# Revit family: Camera-Security-Panasonic-Super_Dynamic-Weatherproof-Network-S1570LSeriesX
name_source: partatom
category: Security Devices
revit_build: Autodesk Revit 2016 (Build: 20150220_1215(x64)
units: mm (PartAtom-declared; Revit-internal decimal feet)

## family parameters
Cut with Voids When Loaded = No
Host = Face
Maintain Annotation Orientation = No
OmniClass Number = 23.85.10.14.11
OmniClass Title = Cameras
Part Type = Normal
Room Calculation Point = No
Round Connector Dimension = Use Diameter
Shared = No

## types (1)
- WV-S1570L
    4K = Resolution : 4K
    Alarm Input Or Output Specification = ALARM IN 1(Alarm input 1/ Black & white input/ Auto time adjustment input) (x1), ALARM IN 2 (Alarm input 2/ ALARM OUT) (x1), ALARM IN 3 (Alarm input 3/ AUX OUT) (x1)
    Angle Of View = 104
    Aspect169 = Yes
    Audio In = Yes
    Audio Out = Yes
    Communication Ports = 10Base-T / 100Base-TX, RJ45 connector
    Date Last Modified = 2019/05/14
    Day Or Night = Yes
    Default Elevation = 0 "
    Description = Security Camera, Super Dynamic, 4K, Weatherproof, Network, WV-S1570L
    Equipment Abbreviation = SC
    Family Version = 1.0.0
    Full HD = Resolution : Full HD
    HFOV Max 169 = 104.00°
    HFOV Max 43 = 104.00°
    HFOV Min 169 = 53.00°
    HFOV Min 43 = 53.00°
    Has POE = Yes
    IP Or Analog = IP
    Indoor Or Outdoor = Outdoor
    Manufacturer = Panasonic
    Minimum Illumination = 0.090 lx
    Model = WV-S1570L
    Model Disclaimer = Contact Panasonic for more information
    Mounting Positions = Mount Dependent or Surface Mount
    Operational Humidity = 10 to 100 % (no condensation)
    Operational Temperature = -40 °F to 140 °F
    Panning Range = -180 to +180
    Part Description = Security Camera, Super Dynamic, 4K, Weatherproof, Network, WV-S1570L
    Part Number = WV-S1570L
    Power Active = 10.0 W
    Product Documentation Link = https://bizpartner.panasonic.net
    Product Material = Paint - Panasonic - Silver
    Product Page URL = https://security.panasonic.com
    Provide Feedback = https://www.surveymonkey.com
    Regulatory Compliance = UL (UL60950-1), c-UL (CSA C22.2 No.60950-1), CE, IEC60950-1, FCC (Part15 ClassA), ICES003 ClassA, EN55032 ClassB, EN55024
    Shock Resistance = IK10 (IEC 62262)
    Storage Temperature = -40 °F to 140 °F
    Super Dynamic Range = Yes
    Tilting Range = -100 to +100
    URL = http://security.panasonic.com
    VFOV Max 169 = 56.00°
    VFOV Max 43 = 56.00°
    VFOV Min 169 = 30.00°
    VFOV Min 43 = 30.00°
    Vandal Resistant = Yes
    Voltage DC = 12 V
    WQHD = Resolution : WQHD
    Water and Dust Resistance = IP66 (IEC60529), Type 4X (UL50E), NEMA 4X compliant
    Width = 5.23622 "
    Yaw Max = 100.00°
    Yaw Min = -190.00°
    Yawing Range = -190 to +100
    z Base Square = Yes
    z Camera Center Offset = 0.2874 "
    z Camera Center Offset Base = 1.1811 "
    z Column Height = 3.11024 "
    z Const CameraYawAxis = 15.74803 "
    z Const Pan Handle Length = 27.55906 "
    z Const Tilt Base Length = 9.84252 "
    z Const Tilt Base2 Length = 19.68504 "
    z Const Tilt Handle Length = 14.17323 "
    z Const Yaw Axis Length = 7.87402 "
    z Const Yaw Base Length = 10.23622 "
    z Const Yaw Base2 Length = 17.32283 "
    z Const Yaw Handle Length = 9.25197 "
    z Hinge Height = 3.79921 "
    z VV Viewpoint Depth Max = 8.2726 "
    z VV Viewpoint Depth Min = 8.2726 "

## geometry (parser evidence)
native form markers: Sweep x13
no freeform markers — native parametric forms only
